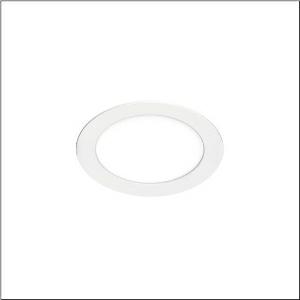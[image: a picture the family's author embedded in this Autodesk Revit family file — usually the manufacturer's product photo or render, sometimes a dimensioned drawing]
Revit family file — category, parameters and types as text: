
# Revit family: lunis_41_flat_51dr10mfhcb
name_source: partatom
category: Lighting Fixtures
units: mm (PartAtom-declared; Revit-internal decimal feet)

## family parameters
Cut with Voids When Loaded = No
Host = Face
Light Source = No
Part Type = Normal
Room Calculation Point = No
Round Connector Dimension = Use Diameter
Shared = No

## types (1)
- --- (1 x LED, 2500 lm, 19.5 W, 6500K)
    Apparent Load = 20 VA
    CIE Flux Codes = 49 80 96 100 100
    Color Rendering = 80
    Color Temperature = 6500K
    Default Elevation = 1800 mm
    Description = Lunis 41 Flat, downlight, light emission: direct distribution, LED rated luminous flux: 2.430lm, light colour: 840/865, mains connection: 230V, AC, 50/60Hz, housing, round, of aluminium, coated, traffic white (RAL 9016), diameter: 225mm, protection rating (complete): IP20, protection rating (on room side): IP44, insulation class (complete): insulation class II (safety insulation), certification: CE, permissible ambient temperature for indoor applications: -20..+40°C, packaging unit: 1 piece
    Height = 0 mm  [stored 0 ft]
    Lamp = 1 x LED
    Lamp Light Flux = 2500 lm
    Lamp Power = 19.5 W
    Lamp count = 1
    Length = 225 mm
    Luminous efficacy = 128 lm/W
    Manufacturer = Siteco
    ModVariant = No
    Model = 51DR10MFHCB
    Mounting Place = Ceiling
    Mounting Type = Recessed
    Number of Poles = 1
    OnlyDefault = Yes
    Power Factor = 1
    Product Name = Lunis 41 Flat
    Product group = downlight
    ProductGroupID = 401
    Protection Class = Protection class II
    Protection Degree = IP 20
    RLX_Detail_Level = 1
    RLX_Emergency_Light_Flux = 0 lm
    RLX_Emergency_Type = 0
    RLX_Emergency_Type_DB = No
    RlxData = <blob elided: 11585 chars, md5=a1a9b8f6>
    Socket = socket
    Standby Power = 0 W
    System Light Flux = 2500 lm
    System Power = 20 W
    Type Comments = individual setting: colour temperature 6500K
    Type Image = l_1340923.jpg
    URL = http://relux.com
    VarID = @adj_020029
    Voltage = 0 V
    Weight = 0.00 kg
    Width = 0 mm  [stored 0 ft]

note: [stored X ft] marks values corroborated as IEEE doubles in the binary element streams (Revit-internal decimal feet)

## geometry (parser evidence)
native form markers: Sweep x9
no freeform markers — native parametric forms only
